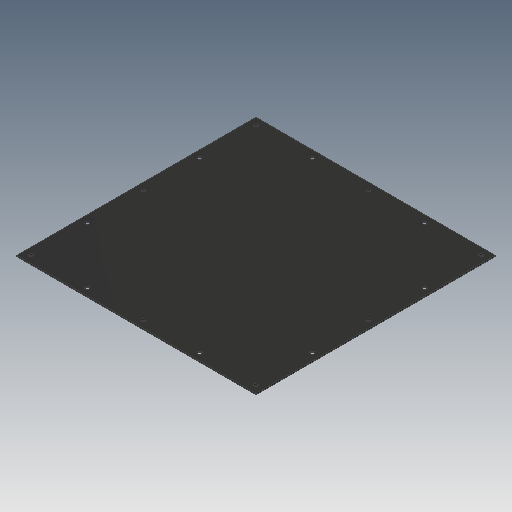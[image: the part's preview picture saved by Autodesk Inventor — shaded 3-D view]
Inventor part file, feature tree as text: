
AUTODESK INVENTOR PART (.ipt)
format: ipt  version: 2018.2 (Build 222227000, 227)  size: 110,592 bytes
history: native  units: mm
features: sketch x2, extrude x1, hole x1, pattern_linear x1, pattern_circular x1, projected_geometry x1
ambient origin geometry x8: Origin, YZ Plane, XZ Plane, XY Plane, X Axis, Y Axis, Z Axis, Center Point
bodies: Solid1 (feature_tree)
feature tree (7):
  extrude  "Extrusion1"  Depth=340.0mm
  hole  "Hole1"  [1 undecoded]
  pattern_linear  "Rectangular Pattern1"  Spacing1=10.0mm  [1 undecoded]
  pattern_circular  "Circular Pattern1"  [2 undecoded]
  sketch  "Sketch1"  dims[d0=340.0mm d1=340.0mm]
  sketch  "Sketch2"  dims[d2=1.5875mm d3=0.0mm d4=10.0mm d5=10.0mm d6=5.5mm d7=6.0mm d8=12.24mm d9=3.58mm d10=90.0deg d11=8.0mm d12=20.594885mm d13=20.0mm d15=320.0mm d16=50.0mm d18=80.0mm d19=20.0mm d20=90.0deg]
  projected_geometry  "Projected Loop1"
note: 4 required parameter values undecoded (feature->parameter linkage not recoverable at this tier; creation-order binding heuristic only, values carry confidence <= 0.55)
